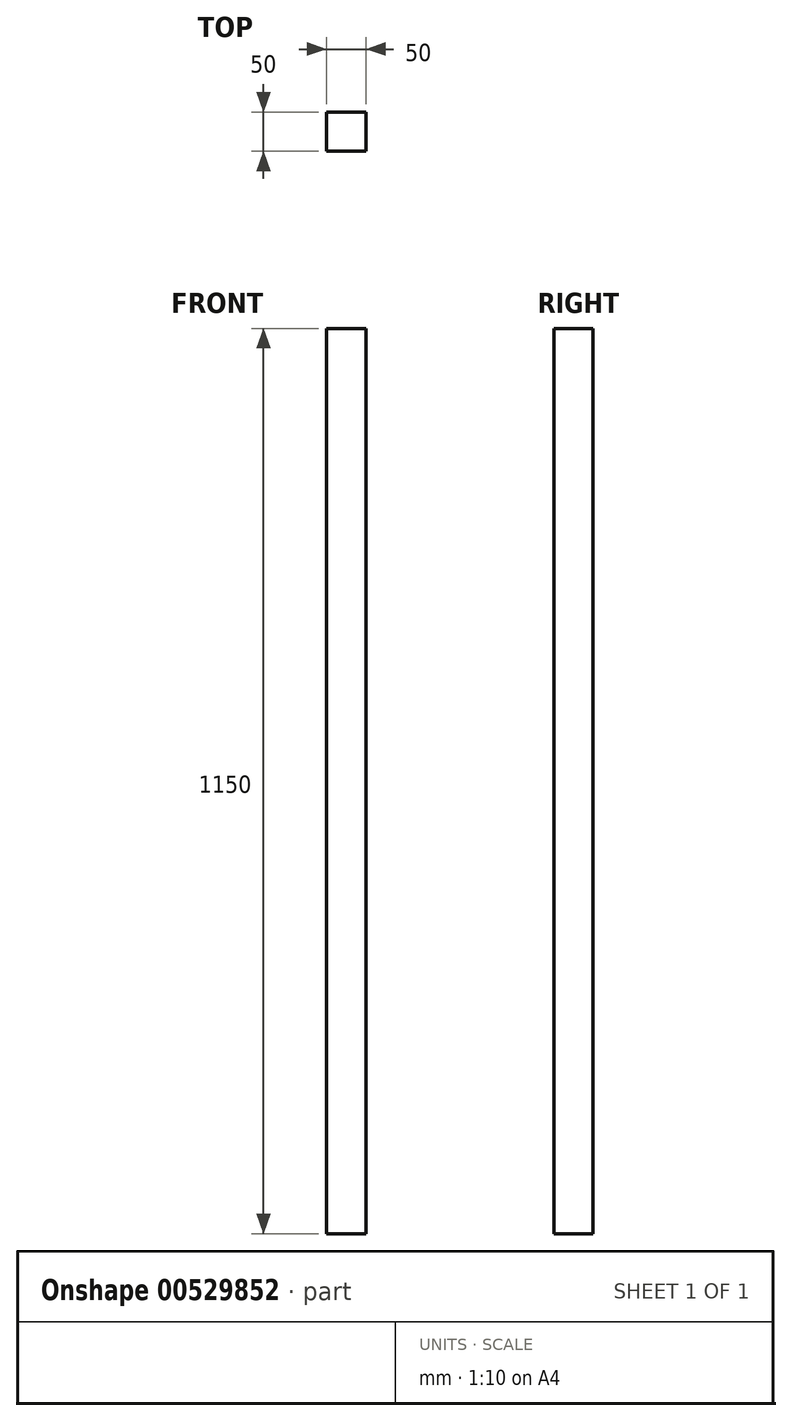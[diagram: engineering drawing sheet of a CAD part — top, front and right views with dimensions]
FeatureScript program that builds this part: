
annotation { "Feature Type Name" : "Feature", "Feature Type Description" : "" }
export const myFeature = defineFeature(function(context is Context, id is Id, definition is map)
    precondition{}
    {
        {
            var Q0;
            Q0=qCreatedBy(makeId("Top.planeOp"),FACE);
            var sketch = newSketch(context, id + "F0", { "sketchPlane" : qUnion([Q0])});
            skLineSegment(sketch, "E0.bottom", {"start": v(-25, -25) * mm, "end": v(25, -25) * mm});
            skLineSegment(sketch, "E0.top", {"start": v(-25, 25) * mm, "end": v(25, 25) * mm});
            skLineSegment(sketch, "E0.left", {"start": v(-25, -25) * mm, "end": v(-25, 25) * mm});
            skLineSegment(sketch, "E0.right", {"start": v(25, -25) * mm, "end": v(25, 25) * mm});
            skPoint(sketch, "E0.middle", {"position": v(0, 0) * mm});
            skSolve(sketch);
        }
        {
            var Q0;
            Q0 = qSketchRegion(id + "F0", true);
            extrude(context, id + "F1", {"entities" : qUnion([Q0]), "depth" : 1150 * mm, "offsetDistance" : 25 * mm});
        }
    });
